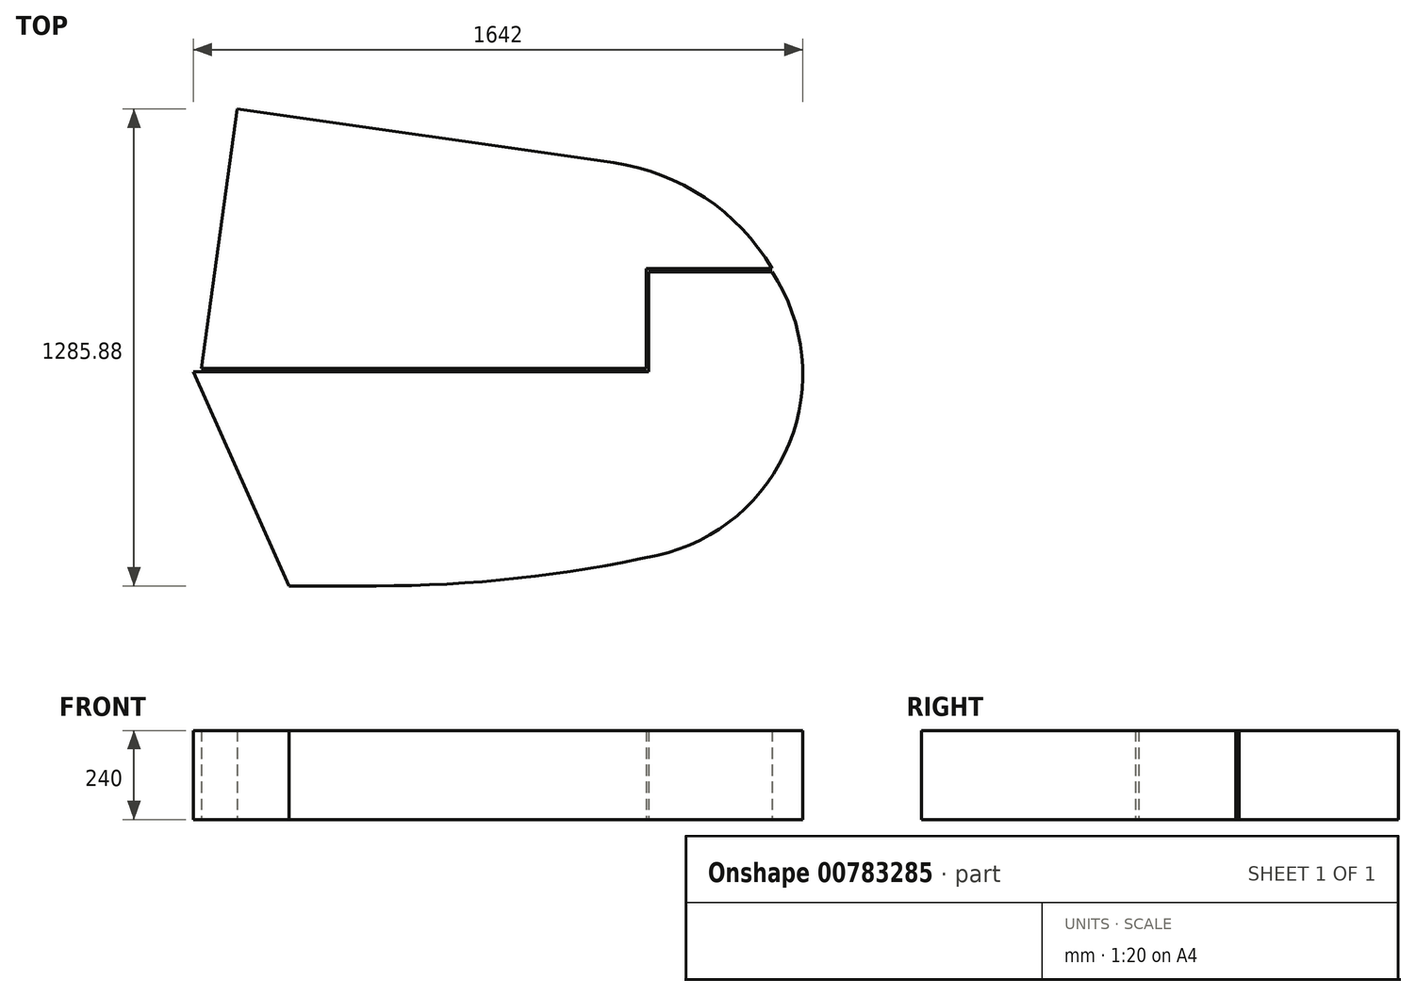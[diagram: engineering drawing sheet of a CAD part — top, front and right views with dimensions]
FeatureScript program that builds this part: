
annotation { "Feature Type Name" : "Feature", "Feature Type Description" : "" }
export const myFeature = defineFeature(function(context is Context, id is Id, definition is map)
    precondition{}
    {
        {
            var Q0;
            Q0=qCreatedBy(makeId("Top.planeOp"),FACE);
            var sketch = newSketch(context, id + "F0", { "sketchPlane" : qUnion([Q0])});
            skLineSegment(sketch, "E0", {"start": v(80, -455) * mm, "end": v(176, 244.88) * mm});
            skLineSegment(sketch, "E1", {"start": v(176, 244.88) * mm, "end": v(1190.78, 100.05) * mm});
            skLineSegment(sketch, "E2", {"start": v(80, -455) * mm, "end": v(1278, -455) * mm});
            skLineSegment(sketch, "E3", {"start": v(1278, -455) * mm, "end": v(1278, -185) * mm});
            skLineSegment(sketch, "E4", {"start": v(1278, -185) * mm, "end": v(1617.34, -185) * mm});
            skArc(sketch, "E5", {"start": v(1617.34, -185) * mm, "mid": v(1436.48, 6.04) * mm, "end": v(1190.78, 100.05) * mm});
            skLineSegment(sketch, "E6", {"start": v(0, 270) * mm, "end": v(0, 0) * mm, "construction": true});
            skLineSegment(sketch, "E7", {"start": v(0, 0) * mm, "end": v(1445.35, 0) * mm, "construction": true});
            skLineSegment(sketch, "E8", {"start": v(176, 244.88) * mm, "end": v(0, 270) * mm, "construction": true});
            skLineSegment(sketch, "E9", {"start": v(0, -1857.77) * mm, "end": v(0, -1250) * mm, "construction": true});
            skLineSegment(sketch, "E10", {"start": v(0, -1250) * mm, "end": v(2482.3, -1250) * mm, "construction": true});
            skLineSegment(sketch, "E11", {"start": v(316, -1801) * mm, "end": v(58, -1224) * mm});
            skLineSegment(sketch, "E12", {"start": v(58, -1224) * mm, "end": v(1285, -1224) * mm});
            skLineSegment(sketch, "E13", {"start": v(1285, -1224) * mm, "end": v(1285, -954) * mm});
            skLineSegment(sketch, "E14", {"start": v(1285, -954) * mm, "end": v(1616.92, -954) * mm});
            skLineSegment(sketch, "E15", {"start": v(316, -1801) * mm, "end": v(551.19, -1801) * mm});
            skArc(sketch, "E16", {"start": v(1308.14, -1718.17) * mm, "mid": v(1663.58, -1417.33) * mm, "end": v(1616.92, -954) * mm});
            skArc(sketch, "E17", {"start": v(551.19, -1801) * mm, "mid": v(931.92, -1780.23) * mm, "end": v(1308.14, -1718.17) * mm});
            skPoint(sketch, "E18", {"position": v(931.92, -1780.23) * mm});
            skSolve(sketch);
        }
        {
            var Q0;
            Q0=makeQuery(id+"F0.imprint","IMPRINT",FACE,{"disambiguationData":[TD([[makeQuery(id+"F0.imprint","IMPRINT",EDGE,{"derivedFrom":sQuery(id+"F0.wireOp",EDGE,"E0")}),-1.0]])]});
            extrude(context, id + "F1", {"entities" : qUnion([Q0]), "depth" : 120 * mm, "offsetDistance" : 25 * mm, "hasSecondDirection" : true, "secondDirectionOppositeDirection" : true, "secondDirectionDepth" : 120 * mm});
        }
        {
            var Q0;
            Q0=makeQuery(id+"F0.imprint","IMPRINT",FACE,{"disambiguationData":[TD([[makeQuery(id+"F0.imprint","IMPRINT",EDGE,{"derivedFrom":sQuery(id+"F0.wireOp",EDGE,"E11")}),-1.0]])]});
            extrude(context, id + "F2", {"entities" : qUnion([Q0]), "depth" : 120 * mm, "offsetDistance" : 25 * mm, "hasSecondDirection" : true, "secondDirectionOppositeDirection" : true, "secondDirectionDepth" : 120 * mm});
        }
        {
            var Q0;
            Q0=makeQuery(id+"F2.opExtrude","SWEPT_BODY",BODY,{"disambiguationData":[OSD([sQuery(id+"F0.wireOp",EDGE,"E11"),sQuery(id+"F0.wireOp",EDGE,"E12"),sQuery(id+"F0.wireOp",EDGE,"E13"),sQuery(id+"F0.wireOp",EDGE,"E14"),sQuery(id+"F0.wireOp",EDGE,"E15"),sQuery(id+"F0.wireOp",EDGE,"E16"),sQuery(id+"F0.wireOp",EDGE,"E17")])]});
            transform(context, id + "F3", {"entities" : qUnion([Q0]), "transformType" : TransformType.TRANSLATION_3D, "dx" : 0 * mm, "dy" : 760 * mm, "dz" : 0 * mm, "makeCopy" : false});
        }
    });
